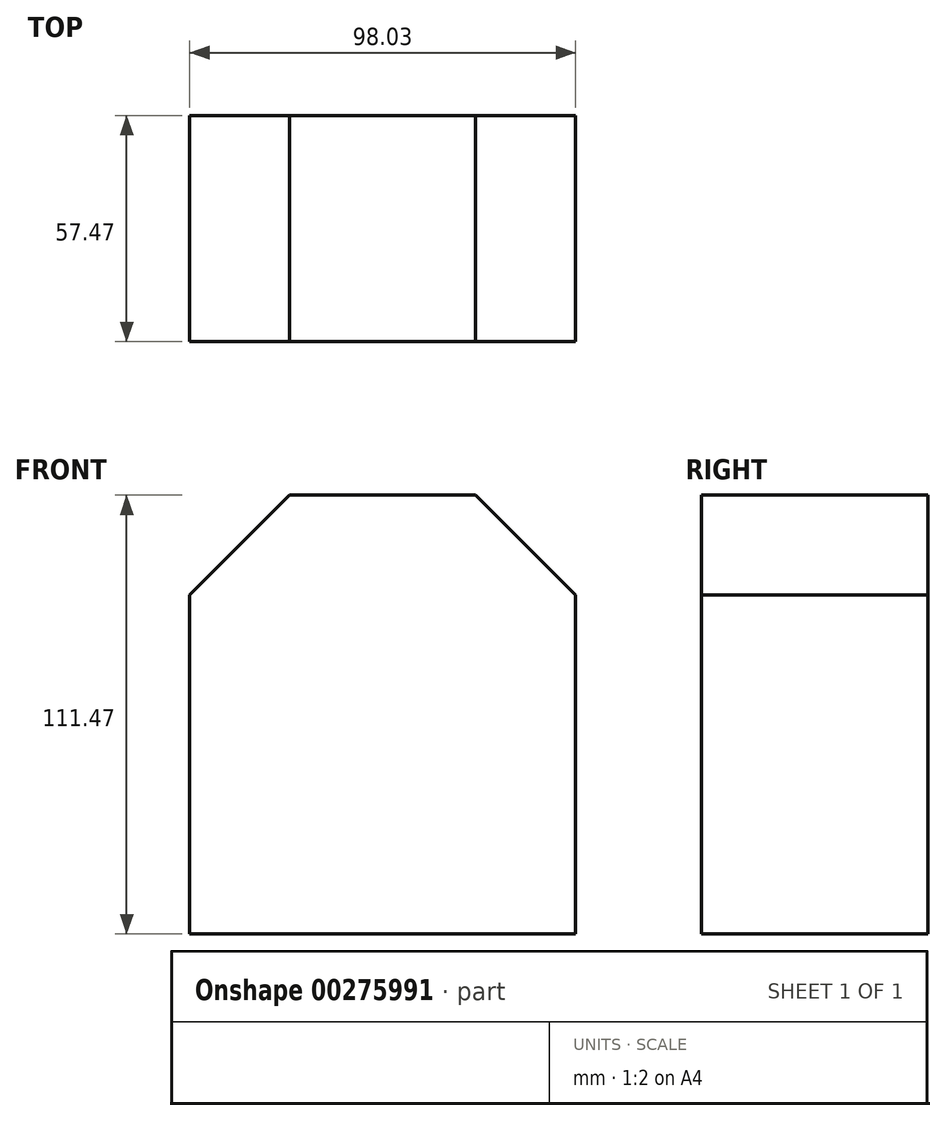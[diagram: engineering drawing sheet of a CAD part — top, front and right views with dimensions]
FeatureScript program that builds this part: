
annotation { "Feature Type Name" : "Feature", "Feature Type Description" : "" }
export const myFeature = defineFeature(function(context is Context, id is Id, definition is map)
    precondition{}
    {
        {
            var Q0;
            Q0=qCreatedBy(makeId("Top.planeOp"),FACE);
            var sketch = newSketch(context, id + "F0", { "sketchPlane" : qUnion([Q0])});
            skLineSegment(sketch, "E0.bottom", {"start": v(-47.27, 0) * mm, "end": v(50.76, 0) * mm});
            skLineSegment(sketch, "E0.top", {"start": v(-47.27, 57.47) * mm, "end": v(50.76, 57.47) * mm});
            skLineSegment(sketch, "E0.left", {"start": v(-47.27, 0) * mm, "end": v(-47.27, 57.47) * mm});
            skLineSegment(sketch, "E0.right", {"start": v(50.76, 0) * mm, "end": v(50.76, 57.47) * mm});
            skSolve(sketch);
        }
        {
            var Q0;
            Q0 = qSketchRegion(id + "F0", true);
            extrude(context, id + "F1", {"entities" : qUnion([Q0]), "depth" : 25.4 * mm});
        }
        {
            var Q0;
            Q0=makeQuery(id+"F1.opExtrude","CAP_EDGE",EDGE,{"disambiguationData":[OSD([sQuery(id+"F0.wireOp",EDGE,"E0.right")])],"isStart":false});
            chamfer(context, id + "F2", {"entities" : qUnion([Q0]), "width" : 25.4 * mm, "tangentPropagation" : true});
        }
        {
            var Q0;
            Q0=makeQuery(id+"F1.opExtrude","CAP_EDGE",EDGE,{"disambiguationData":[OSD([sQuery(id+"F0.wireOp",EDGE,"E0.left")])],"isStart":false});
            chamfer(context, id + "F3", {"entities" : qUnion([Q0]), "width" : 25.4 * mm, "tangentPropagation" : true});
        }
        {
            var Q0;
            Q0=makeQuery(id+"F1.opExtrude","CAP_FACE",FACE,{"disambiguationData":[OSD([sQuery(id+"F0.wireOp",EDGE,"E0.bottom"),sQuery(id+"F0.wireOp",EDGE,"E0.top"),sQuery(id+"F0.wireOp",EDGE,"E0.left"),sQuery(id+"F0.wireOp",EDGE,"E0.right")])],"isStart":true});
            extrude(context, id + "F4", {"entities" : qUnion([Q0]), "operationType" : NewBodyOperationType.ADD, "depth" : 86.07 * mm});
        }
    });
